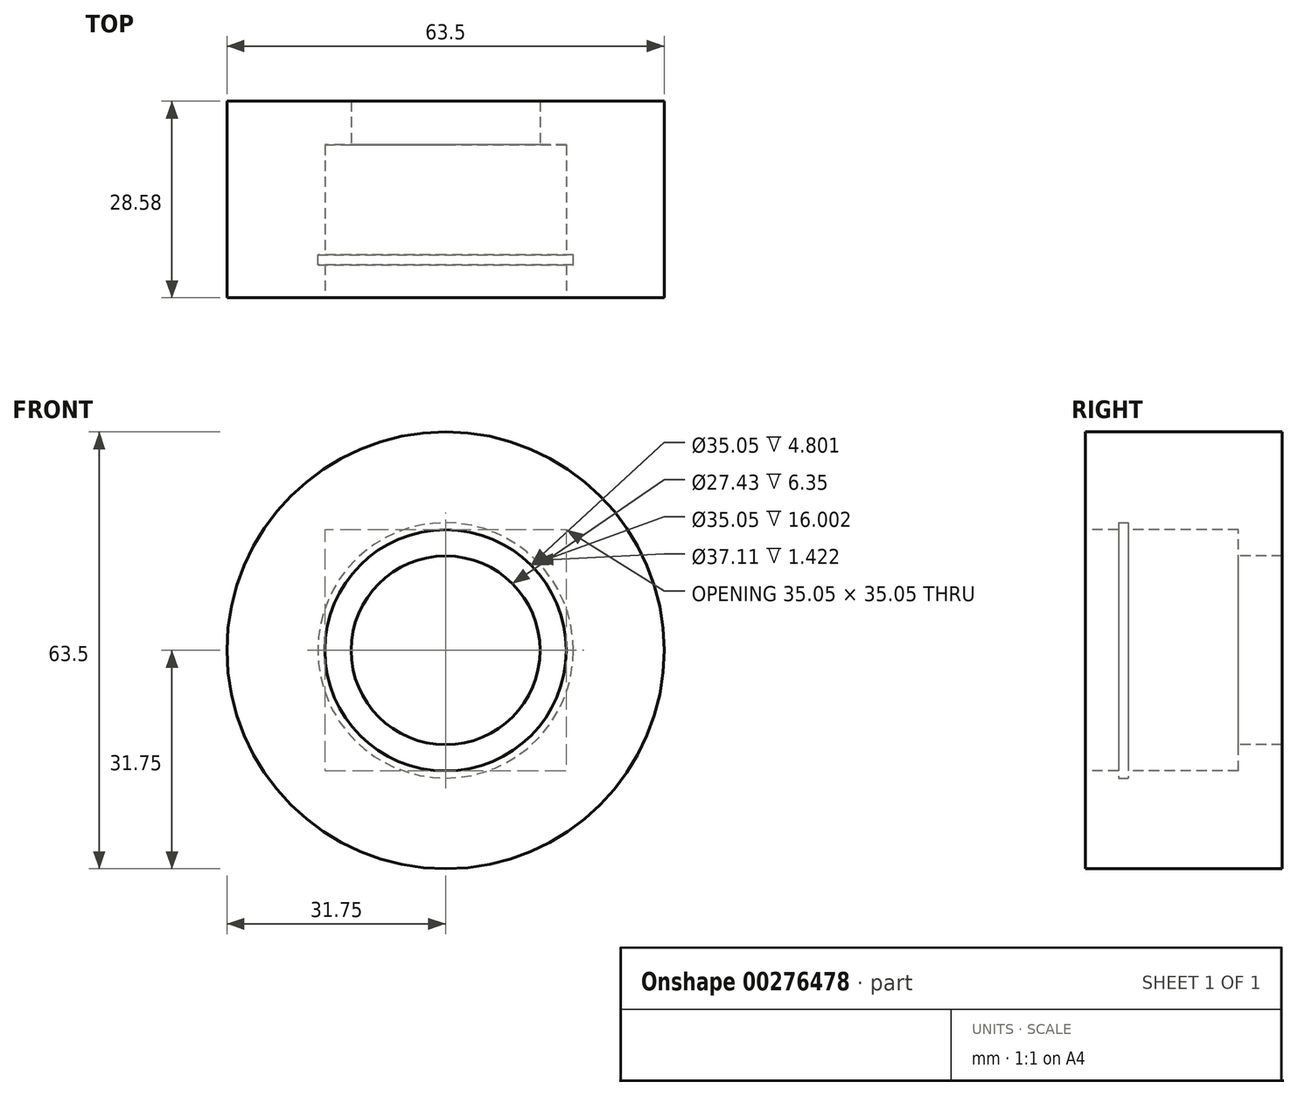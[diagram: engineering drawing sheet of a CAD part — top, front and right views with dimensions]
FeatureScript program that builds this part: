
annotation { "Feature Type Name" : "Feature", "Feature Type Description" : "" }
export const myFeature = defineFeature(function(context is Context, id is Id, definition is map)
    precondition{}
    {
        {
            var Q0;
            Q0=qCreatedBy(makeId("Front.planeOp"),FACE);
            var sketch = newSketch(context, id + "F0", { "sketchPlane" : qUnion([Q0])});
            skCircle(sketch, "E0", {"center": v(0, 0) * mm, "radius": 31.75 * mm});
            skSolve(sketch);
        }
        {
            var Q0;
            Q0=makeQuery(id+"F0.imprint","IMPRINT",FACE,{"disambiguationData":[TD([[makeQuery(id+"F0.imprint","IMPRINT",EDGE,{"derivedFrom":sQuery(id+"F0.wireOp",EDGE,"E0")}),1.0]])]});
            extrude(context, id + "F1", {"entities" : qUnion([Q0]), "depth" : 28.57 * mm});
        }
        {
            var Q0;
            Q0=makeQuery(id+"F1.opExtrude","CAP_FACE",FACE,{"disambiguationData":[OSD([sQuery(id+"F0.wireOp",EDGE,"E0")])],"isStart":false});
            var sketch = newSketch(context, id + "F2", { "sketchPlane" : qUnion([Q0])});
            skPoint(sketch, "E1", {"position": v(0, 0) * mm});
            skSolve(sketch);
        }
        {
            var Q0;
            Q0=sQuery(id+"F2.wireOp",VERTEX,"E1");
            var Q1;
            Q1=makeQuery(id+"F1.opExtrude","SWEPT_BODY",BODY,{"disambiguationData":[OSD([sQuery(id+"F0.wireOp",EDGE,"E0")])]});
            hole(context, id + "F3", {"style" : HoleStyle.C_BORE, "endStyle" : HoleEndStyle.THROUGH, "holeDiameter" : 27.43 * mm, "cBoreDiameter" : 35.05 * mm, "cBoreDepth" : 22.22 * mm, "tappedDepth" : 12.7 * mm, "tapClearance" : 3, "locations" : qUnion([Q0]), "scope" : qUnion([Q1])});
        }
        {
            var Q0;
            Q0=qCreatedBy(makeId("Top.planeOp"),FACE);
            var sketch = newSketch(context, id + "F4", { "sketchPlane" : qUnion([Q0])});
            skLineSegment(sketch, "E2.bottom", {"start": v(7.3, -22.35) * mm, "end": v(18.55, -22.35) * mm});
            skLineSegment(sketch, "E2.top", {"start": v(7.3, -23.77) * mm, "end": v(18.55, -23.77) * mm});
            skLineSegment(sketch, "E2.left", {"start": v(7.3, -22.35) * mm, "end": v(7.3, -23.77) * mm});
            skLineSegment(sketch, "E2.right", {"start": v(18.55, -22.35) * mm, "end": v(18.55, -23.77) * mm});
            skLineSegment(sketch, "E3", {"start": v(0, 0) * mm, "end": v(0, 5.2) * mm});
            skSolve(sketch);
        }
        {
            var Q0;
            Q0=makeQuery(id+"F4.imprint","IMPRINT",FACE,{"disambiguationData":[TD([[makeQuery(id+"F4.imprint","IMPRINT",EDGE,{"derivedFrom":sQuery(id+"F4.wireOp",EDGE,"E2.bottom")}),-1.0]])]});
            var Q1;
            Q1=sQuery(id+"F4.wireOp",EDGE,"E3");
            revolve(context, id + "F5", {"operationType" : NewBodyOperationType.REMOVE, "entities" : qUnion([Q0]), "axis" : qUnion([Q1]), "revolveType" : RevolveType.FULL, "oppositeDirection" : true});
        }
    });
